# Revit family: 20. 5er Set Wichmann TW90 Faltbox EF
name_source: partatom
category: HLS-Bauteile
revit_build: Autodesk Revit 2018 (Build: 20170223_1515(x64)
units: mm (PartAtom-declared; Revit-internal decimal feet)

## family parameters
Basisbauteil = Wand
Beim Laden mit Abzugskörper schneiden = Nein
Bemaßung runder Anschluss = Durchmesser verwenden
Gemeinsam genutzt = Nein
Immer vertikal = Ja
Raumberechnungspunkt = Nein
Teiletyp = Normal

## types (10) — shared parameters
Abst = 45 mm
Höhe = 1725 mm
Höhe Außenmaß = 60 mm  [stored 0.19685 ft]
Höhe Innenmaß = 35 mm  [stored 0.114829 ft]
Höhe Rohbauöffnung = 90 mm  [stored 0.295276 ft]
Höhe UK Durchbruch = 1680 mm
Rohbauöffnung = Ja

## per-type parameters (varying)
| type | Bautiefe | Breite Außenmaß | Breite Innenmaß | Breite Rohbauöffnung | HAN |
| 5er Set TW90 Faltbox EF, 60x160x150 mm | 150 mm  [stored 0.492126 ft] | 160 mm | 130 mm | 180 mm | VEFFB60160150 |
| 5er Set TW90 Faltbox EF, 60x240x150 mm | 150 mm  [stored 0.492126 ft] | 240 mm | 210 mm | 260 mm | VEFFB60240150 |
| 5er Set TW90 Faltbox EF, 60x280x125 mm | 125 mm  [stored 0.410105 ft] | 280 mm | 250 mm | 300 mm | VEFFB60280125 |
| 5er Set TW90 Faltbox EF, 60x280x150 mm | 150 mm  [stored 0.492126 ft] | 280 mm | 250 mm | 300 mm | VEFFB60280150 |
| 5er Set TW90 Faltbox EF, 60x120x125 mm | 125 mm  [stored 0.410105 ft] | 120 mm  [stored 0.393701 ft] | 90 mm  [stored 0.295276 ft] | 140 mm  [stored 0.459318 ft] | VEFFB60120125 |
| 5er Set TW90 Faltbox EF, 60x120x150 mm | 150 mm  [stored 0.492126 ft] | 120 mm  [stored 0.393701 ft] | 90 mm  [stored 0.295276 ft] | 140 mm  [stored 0.459318 ft] | VEFFB60120150 |
| 5er Set TW90 Faltbox EF, 60x160x125 mm | 125 mm  [stored 0.410105 ft] | 160 mm | 130 mm | 180 mm | VEFFB60160125 |
| 5er Set TW90 Faltbox EF, 60x200x125 mm | 125 mm  [stored 0.410105 ft] | 200 mm  [stored 0.656168 ft] | 170 mm | 220 mm | VEFFB60200125 |
| 5er Set TW90 Faltbox EF, 60x200x150 mm | 150 mm  [stored 0.492126 ft] | 200 mm  [stored 0.656168 ft] | 170 mm | 220 mm | VEFFB60200150 |
| 5er Set TW90 Faltbox EF, 60x240x125 mm | 125 mm  [stored 0.410105 ft] | 240 mm | 210 mm | 260 mm | VEFFB60240125 |

note: [stored X ft] marks values corroborated as IEEE doubles in the binary element streams (Revit-internal decimal feet)
